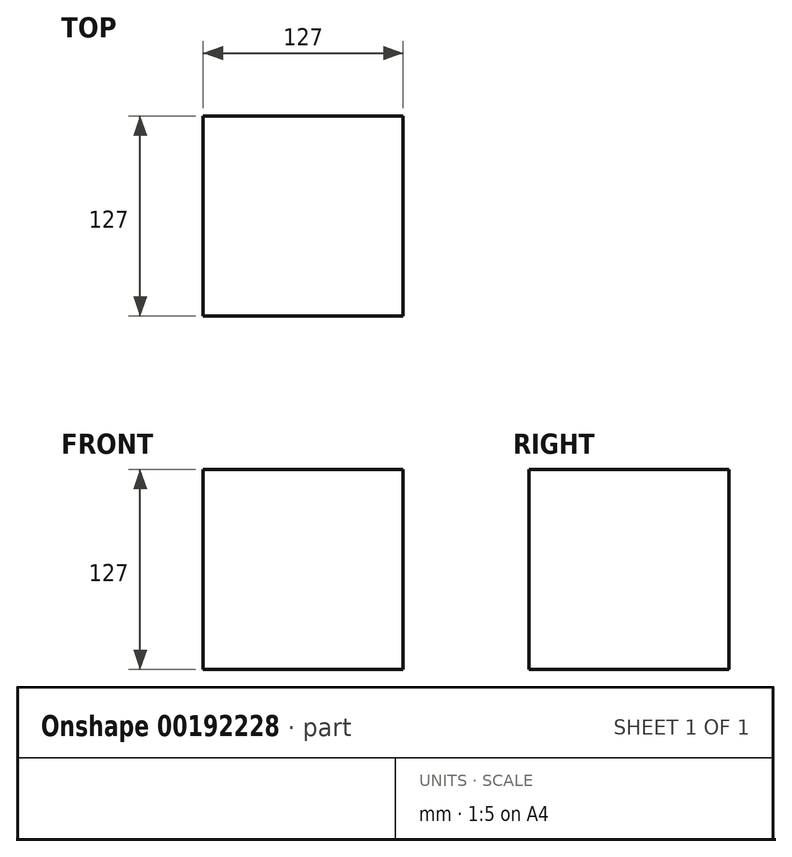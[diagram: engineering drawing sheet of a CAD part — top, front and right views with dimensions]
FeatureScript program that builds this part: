
annotation { "Feature Type Name" : "Feature", "Feature Type Description" : "" }
export const myFeature = defineFeature(function(context is Context, id is Id, definition is map)
    precondition{}
    {
        {
            var Q0;
            Q0=qCreatedBy(makeId("Front.planeOp"),FACE);
            var sketch = newSketch(context, id + "F0", { "sketchPlane" : qUnion([Q0])});
            skLineSegment(sketch, "E0.bottom", {"start": v(63.5, 63.5) * mm, "end": v(-63.5, 63.5) * mm});
            skLineSegment(sketch, "E0.top", {"start": v(63.5, -63.5) * mm, "end": v(-63.5, -63.5) * mm});
            skLineSegment(sketch, "E0.left", {"start": v(63.5, 63.5) * mm, "end": v(63.5, -63.5) * mm});
            skLineSegment(sketch, "E0.right", {"start": v(-63.5, 63.5) * mm, "end": v(-63.5, -63.5) * mm});
            skPoint(sketch, "E0.middle", {"position": v(0, 0) * mm});
            skSolve(sketch);
        }
        {
            var Q0;
            Q0=makeQuery(id+"F0.imprint","IMPRINT",FACE,{"disambiguationData":[TD([[makeQuery(id+"F0.imprint","IMPRINT",EDGE,{"derivedFrom":sQuery(id+"F0.wireOp",EDGE,"E0.bottom")}),1.0]])]});
            extrude(context, id + "F1", {"entities" : qUnion([Q0]), "oppositeDirection" : true, "depth" : 127 * mm});
        }
    });
